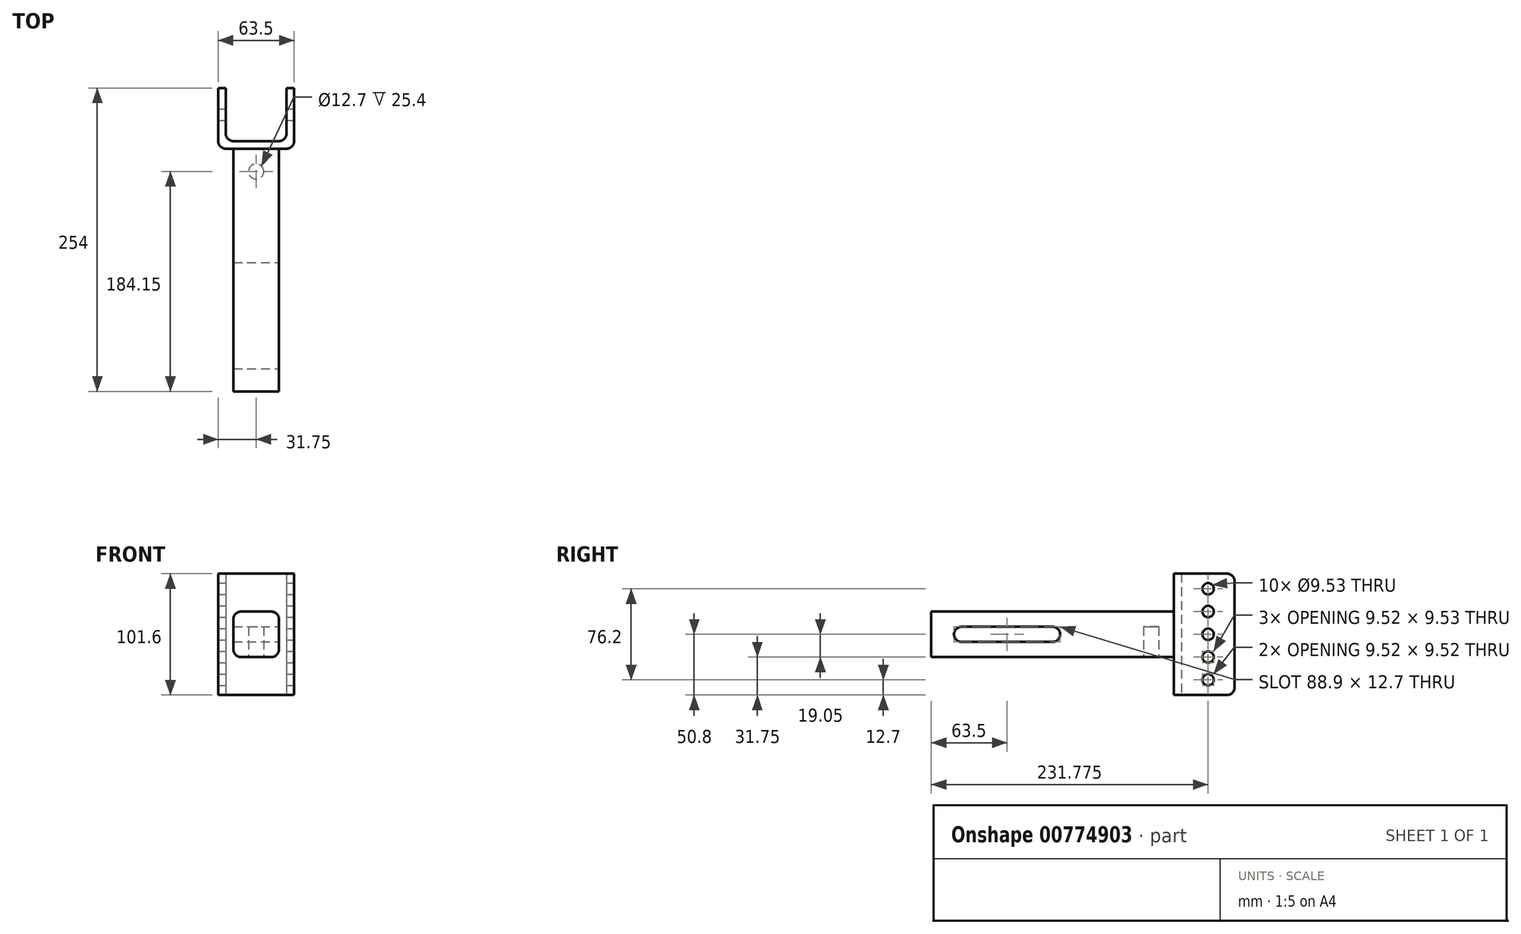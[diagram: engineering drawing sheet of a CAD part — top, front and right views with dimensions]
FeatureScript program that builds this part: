
annotation { "Feature Type Name" : "Feature", "Feature Type Description" : "" }
export const myFeature = defineFeature(function(context is Context, id is Id, definition is map)
    precondition{}
    {
        {
            var Q0;
            Q0=qCreatedBy(makeId("Front.planeOp"),FACE);
            var sketch = newSketch(context, id + "F0", { "sketchPlane" : qUnion([Q0])});
            skLineSegment(sketch, "E0.bottom", {"start": v(12.7, -19.05) * mm, "end": v(-12.7, -19.05) * mm});
            skLineSegment(sketch, "E0.top", {"start": v(12.7, 19.05) * mm, "end": v(-12.7, 19.05) * mm});
            skLineSegment(sketch, "E0.left", {"start": v(19.05, -12.7) * mm, "end": v(19.05, 12.7) * mm});
            skLineSegment(sketch, "E0.right", {"start": v(-19.05, -12.7) * mm, "end": v(-19.05, 12.7) * mm});
            skPoint(sketch, "E0.middle", {"position": v(0, 0) * mm});
            skPoint(sketch, "E1.visualSharp", {"position": v(-19.05, -19.05) * mm});
            skArc(sketch, "E1.filletArc", {"start": v(-19.05, -12.7) * mm, "mid": v(-17.2, -17.2) * mm, "end": v(-12.7, -19.05) * mm});
            skPoint(sketch, "E2.visualSharp", {"position": v(19.05, -19.05) * mm});
            skArc(sketch, "E2.filletArc", {"start": v(12.7, -19.05) * mm, "mid": v(17.2, -17.2) * mm, "end": v(19.05, -12.7) * mm});
            skPoint(sketch, "E3.visualSharp", {"position": v(19.05, 19.05) * mm});
            skArc(sketch, "E3.filletArc", {"start": v(19.05, 12.7) * mm, "mid": v(17.2, 17.2) * mm, "end": v(12.7, 19.05) * mm});
            skPoint(sketch, "E4.visualSharp", {"position": v(-19.05, 19.05) * mm});
            skArc(sketch, "E4.filletArc", {"start": v(-12.7, 19.05) * mm, "mid": v(-17.2, 17.2) * mm, "end": v(-19.05, 12.7) * mm});
            skSolve(sketch);
        }
        {
            var Q0;
            Q0 = qSketchRegion(id + "F0", true);
            extrude(context, id + "F1", {"entities" : qUnion([Q0]), "depth" : 203.2 * mm, "offsetDistance" : 25.4 * mm});
        }
        {
            var Q0;
            Q0=makeQuery(id+"F1.opExtrude","SWEPT_FACE",FACE,{"disambiguationData":[OSD([sQuery(id+"F0.wireOp",EDGE,"E0.left")])]});
            var sketch = newSketch(context, id + "F2", { "sketchPlane" : qUnion([Q0])});
            skPoint(sketch, "E5.centerSnap0", {"position": v(-101.6, 12.7) * mm});
            skLineSegment(sketch, "E6", {"start": v(-33.6, 6.35) * mm, "end": v(-33.6, 6.35) * mm});
            skPoint(sketch, "E7.center.orphan", {"position": v(-33.6, 0) * mm});
            skPoint(sketch, "E8.start.orphan", {"position": v(-33.6, -6.35) * mm});
            skPoint(sketch, "E5.center.orphan", {"position": v(-101.6, 0) * mm});
            skPoint(sketch, "E9.start.orphan", {"position": v(-101.6, 6.35) * mm});
            skArc(sketch, "E10", {"start": v(-101.6, -6.35) * mm, "mid": v(-95.25, 0) * mm, "end": v(-101.6, 6.35) * mm});
            skArc(sketch, "E11", {"start": v(-177.8, 6.35) * mm, "mid": v(-184.15, 0) * mm, "end": v(-177.8, -6.35) * mm});
            skLineSegment(sketch, "E12", {"start": v(-101.6, 6.35) * mm, "end": v(-177.8, 6.35) * mm});
            skLineSegment(sketch, "E13", {"start": v(-101.6, -6.35) * mm, "end": v(-177.8, -6.35) * mm});
            skSolve(sketch);
        }
        {
            var Q0;
            Q0 = qSketchRegion(id + "F2", true);
            extrude(context, id + "F3", {"entities" : qUnion([Q0]), "operationType" : NewBodyOperationType.REMOVE, "oppositeDirection" : true, "depth" : 38.1 * mm, "offsetDistance" : 25.4 * mm});
        }
        {
            var Q0;
            Q0=qCreatedBy(makeId("Top.planeOp"),FACE);
            var sketch = newSketch(context, id + "F4", { "sketchPlane" : qUnion([Q0])});
            skLineSegment(sketch, "E14.bottom", {"start": v(-25.4, 0) * mm, "end": v(25.4, 0) * mm});
            skLineSegment(sketch, "E14.top", {"start": v(-31.75, 50.8) * mm, "end": v(-25.4, 50.8) * mm});
            skLineSegment(sketch, "E14.left", {"start": v(-31.75, 6.35) * mm, "end": v(-31.75, 50.8) * mm});
            skLineSegment(sketch, "E14.right", {"start": v(31.75, 6.35) * mm, "end": v(31.75, 50.8) * mm});
            skPoint(sketch, "E14.middle", {"position": v(0, 25.4) * mm});
            skLineSegment(sketch, "E15.0", {"start": v(-25.4, 12.7) * mm, "end": v(-25.4, 50.8) * mm});
            skLineSegment(sketch, "E15.1", {"start": v(-19.05, 6.35) * mm, "end": v(19.05, 6.35) * mm});
            skLineSegment(sketch, "E15.2", {"start": v(25.4, 12.7) * mm, "end": v(25.4, 50.8) * mm});
            skLineSegment(sketch, "E16.trimOffspring", {"start": v(25.4, 50.8) * mm, "end": v(31.75, 50.8) * mm});
            skPoint(sketch, "E17.visualSharp", {"position": v(25.4, 6.35) * mm});
            skArc(sketch, "E17.filletArc", {"start": v(19.05, 6.35) * mm, "mid": v(23.54, 8.2) * mm, "end": v(25.4, 12.7) * mm});
            skPoint(sketch, "E18.visualSharp", {"position": v(31.75, 0) * mm});
            skArc(sketch, "E18.filletArc", {"start": v(25.4, 0) * mm, "mid": v(29.9, 1.86) * mm, "end": v(31.75, 6.35) * mm});
            skPoint(sketch, "E19.visualSharp", {"position": v(-25.4, 6.35) * mm});
            skArc(sketch, "E19.filletArc", {"start": v(-25.4, 12.7) * mm, "mid": v(-23.54, 8.2) * mm, "end": v(-19.05, 6.35) * mm});
            skPoint(sketch, "E20.visualSharp", {"position": v(-31.75, 0) * mm});
            skArc(sketch, "E20.filletArc", {"start": v(-31.75, 6.35) * mm, "mid": v(-29.9, 1.86) * mm, "end": v(-25.4, 0) * mm});
            skSolve(sketch);
        }
        {
            var Q0;
            Q0=makeQuery(id+"F4.imprint","IMPRINT",FACE,{"disambiguationData":[TD([[makeQuery(id+"F4.imprint","IMPRINT",EDGE,{"derivedFrom":sQuery(id+"F4.wireOp",EDGE,"E14.bottom")}),1.0]])]});
            extrude(context, id + "F5", {"entities" : qUnion([Q0]), "operationType" : NewBodyOperationType.ADD, "depth" : 50.8 * mm, "offsetDistance" : 25.4 * mm});
        }
        {
            var Q0;
            Q0=makeQuery(id+"F5.opExtrude","CAP_FACE",FACE,{"disambiguationData":[OSD([sQuery(id+"F4.wireOp",EDGE,"E14.bottom"),sQuery(id+"F4.wireOp",EDGE,"E14.top"),sQuery(id+"F4.wireOp",EDGE,"E14.left"),sQuery(id+"F4.wireOp",EDGE,"E14.right"),sQuery(id+"F4.wireOp",EDGE,"E15.0"),sQuery(id+"F4.wireOp",EDGE,"E15.1"),sQuery(id+"F4.wireOp",EDGE,"E15.2"),sQuery(id+"F4.wireOp",EDGE,"E16.trimOffspring"),sQuery(id+"F4.wireOp",EDGE,"E17.filletArc"),sQuery(id+"F4.wireOp",EDGE,"E18.filletArc"),sQuery(id+"F4.wireOp",EDGE,"E19.filletArc"),sQuery(id+"F4.wireOp",EDGE,"E20.filletArc")])],"isStart":true});
            extrude(context, id + "F6", {"entities" : qUnion([Q0]), "operationType" : NewBodyOperationType.ADD, "depth" : 50.8 * mm, "offsetDistance" : 25.4 * mm});
        }
        {
            var Q0;
            {var subQ0=sQuery(id+"F4.wireOp",EDGE,"E14.right");Q0=makeQuery(id+"F6.boolean.opBoolean","MERGE",FACE,{"derivedFrom":[makeQuery(id+"F5.opExtrude","SWEPT_FACE",FACE,{"disambiguationData":[OSD([subQ0])]}),makeQuery(id+"F6.opExtrude","SWEPT_FACE",FACE,{"disambiguationData":[OSD([subQ0])]})]});}
            var sketch = newSketch(context, id + "F7", { "sketchPlane" : qUnion([Q0])});
            skCircle(sketch, "E21", {"center": v(28.57, 38.1) * mm, "radius": 4.76 * mm});
            skPoint(sketch, "E21.centerSnap0", {"position": v(28.57, 50.8) * mm});
            skCircle(sketch, "E22.0.1.0", {"center": v(28.57, 19.05) * mm, "radius": 4.76 * mm});
            skCircle(sketch, "E22.0.2.0", {"center": v(28.57, 0) * mm, "radius": 4.76 * mm});
            skCircle(sketch, "E22.0.3.0", {"center": v(28.57, -19.05) * mm, "radius": 4.76 * mm});
            skCircle(sketch, "E22.0.4.0", {"center": v(28.57, -38.1) * mm, "radius": 4.76 * mm});
            skLineSegment(sketch, "E22.direction1", {"start": v(28.57, 38.1) * mm, "end": v(53.97, 38.1) * mm, "construction": true});
            skLineSegment(sketch, "E22.direction2", {"start": v(28.57, 38.1) * mm, "end": v(28.57, 19.05) * mm, "construction": true});
            skSolve(sketch);
        }
        {
            var Q0;
            Q0 = qSketchRegion(id + "F7", true);
            extrude(context, id + "F8", {"entities" : qUnion([Q0]), "operationType" : NewBodyOperationType.REMOVE, "oppositeDirection" : true, "depth" : 63.5 * mm, "offsetDistance" : 25.4 * mm});
        }
        {
            var Q0;
            Q0=makeQuery(id+"F5.opExtrude","CAP_EDGE",EDGE,{"disambiguationData":[OSD([sQuery(id+"F4.wireOp",EDGE,"E16.trimOffspring")])],"isStart":false});
            var Q1;
            Q1=makeQuery(id+"F5.opExtrude","CAP_EDGE",EDGE,{"disambiguationData":[OSD([sQuery(id+"F4.wireOp",EDGE,"E14.top")])],"isStart":false});
            var Q2;
            Q2=makeQuery(id+"F6.opExtrude","CAP_EDGE",EDGE,{"disambiguationData":[OSD([sQuery(id+"F4.wireOp",EDGE,"E14.top")])],"isStart":false});
            var Q3;
            Q3=makeQuery(id+"F6.opExtrude","CAP_EDGE",EDGE,{"disambiguationData":[OSD([sQuery(id+"F4.wireOp",EDGE,"E16.trimOffspring")])],"isStart":false});
            fillet(context, id + "F9", {"entities" : qUnion([Q0, Q1, Q2, Q3]), "radius" : 6.35 * mm, "tangentPropagation" : true, "allowEdgeOverflow" : false});
        }
        {
            var Q0;
            Q0=makeQuery(id+"F1.opExtrude","SWEPT_FACE",FACE,{"disambiguationData":[OSD([sQuery(id+"F0.wireOp",EDGE,"E0.bottom")])]});
            var sketch = newSketch(context, id + "F10", { "sketchPlane" : qUnion([Q0])});
            skCircle(sketch, "E23", {"center": v(0, 19.05) * mm, "radius": 6.35 * mm});
            skSolve(sketch);
        }
        {
            var Q0;
            Q0 = qSketchRegion(id + "F10", true);
            var Q1;
            Q1=sQuery(id+"F10.wireOp",EDGE,"E23");
            extrude(context, id + "F11", {"entities" : qUnion([Q0]), "operationType" : NewBodyOperationType.REMOVE, "surfaceEntities" : qUnion([Q1]), "oppositeDirection" : true, "depth" : 25.4 * mm, "offsetDistance" : 25.4 * mm});
        }
    });
